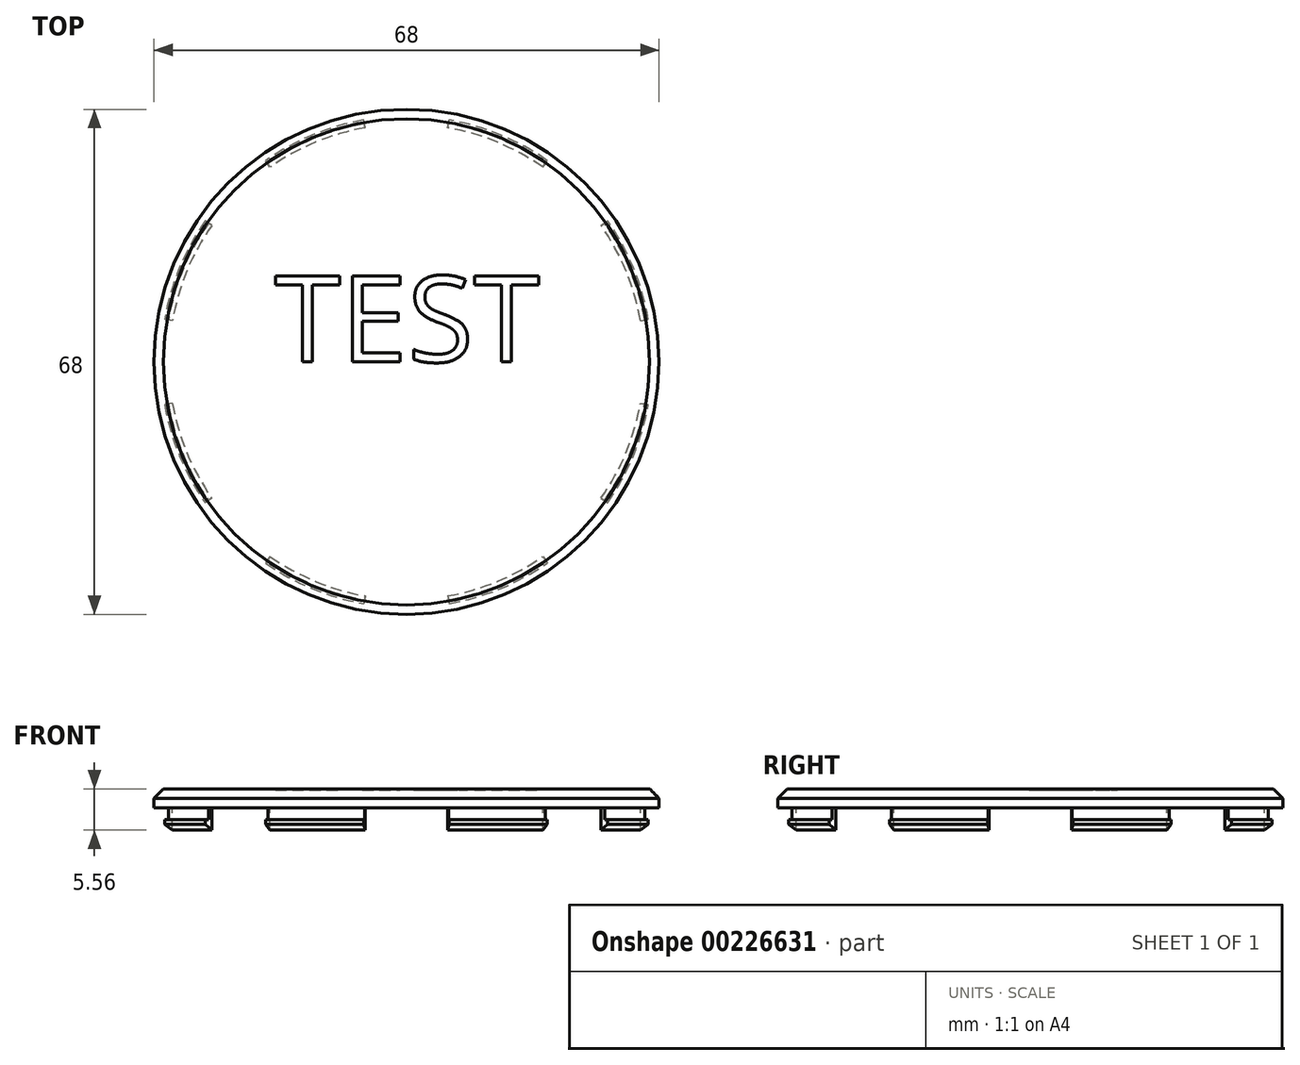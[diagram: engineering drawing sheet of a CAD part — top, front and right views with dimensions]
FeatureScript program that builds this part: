
annotation { "Feature Type Name" : "Feature", "Feature Type Description" : "" }
export const myFeature = defineFeature(function(context is Context, id is Id, definition is map)
    precondition{}
    {
        {
            var Q0;
            Q0=qCreatedBy(makeId("Top.planeOp"),FACE);
            var sketch = newSketch(context, id + "F0", { "sketchPlane" : qUnion([Q0])});
            skCircle(sketch, "E0", {"center": v(0, 0) * mm, "radius": 34 * mm});
            skSolve(sketch);
        }
        {
            var Q0;
            Q0=makeQuery(id+"F0.imprint","IMPRINT",FACE,{"disambiguationData":[TD([[makeQuery(id+"F0.imprint","IMPRINT",EDGE,{"derivedFrom":sQuery(id+"F0.wireOp",EDGE,"E0")}),1.0]])]});
            extrude(context, id + "F1", {"entities" : qUnion([Q0]), "depth" : 2.54 * mm});
        }
        {
            var Q0;
            Q0=makeQuery(id+"F1.opExtrude","CAP_EDGE",EDGE,{"disambiguationData":[OSD([sQuery(id+"F0.wireOp",EDGE,"E0")])],"isStart":false});
            chamfer(context, id + "F2", {"entities" : qUnion([Q0]), "width" : 1.27 * mm, "tangentPropagation" : true});
        }
        {
            var Q0;
            Q0=qCreatedBy(makeId("Front.planeOp"),FACE);
            var sketch = newSketch(context, id + "F3", { "sketchPlane" : qUnion([Q0])});
            skLineSegment(sketch, "E1", {"start": v(32.56, 0) * mm, "end": v(32.56, -1.61) * mm});
            skLineSegment(sketch, "E2", {"start": v(32.56, -1.61) * mm, "end": v(33.07, -1.61) * mm});
            skLineSegment(sketch, "E3", {"start": v(33.07, -1.61) * mm, "end": v(33.07, -2.24) * mm});
            skLineSegment(sketch, "E4", {"start": v(33.07, -2.24) * mm, "end": v(32, -3.02) * mm});
            skLineSegment(sketch, "E5", {"start": v(32, -3.02) * mm, "end": v(32, 0) * mm});
            skLineSegment(sketch, "E6", {"start": v(32, 0) * mm, "end": v(32.56, 0) * mm});
            skLineSegment(sketch, "E7", {"start": v(0, 0) * mm, "end": v(0, -19.48) * mm, "construction": true});
            skSolve(sketch);
        }
        {
            var Q0;
            Q0=qSketchRegion(id+"F3",true);
            var Q1;
            Q1=sQuery(id+"F3.wireOp",EDGE,"E7");
            revolve(context, id + "F4", {"operationType" : NewBodyOperationType.ADD, "entities" : qUnion([Q0]), "axis" : qUnion([Q1]), "revolveType" : RevolveType.FULL});
        }
        {
            var Q0;
            Q0=qCreatedBy(makeId("Top.planeOp"),FACE);
            var sketch = newSketch(context, id + "F5", { "sketchPlane" : qUnion([Q0])});
            skLineSegment(sketch, "E8", {"start": v(0, 0) * mm, "end": v(6.04, 34.27) * mm, "construction": true});
            skLineSegment(sketch, "E9", {"start": v(0, 0) * mm, "end": v(-6.04, 34.27) * mm, "construction": true});
            skLineSegment(sketch, "E10", {"start": v(0, 0) * mm, "end": v(-6.04, 34.27) * mm});
            skLineSegment(sketch, "E11", {"start": v(0, 0) * mm, "end": v(6.04, 34.27) * mm});
            skArc(sketch, "E12", {"start": v(6.04, 34.27) * mm, "mid": v(0, 34.8) * mm, "end": v(-6.04, 34.27) * mm});
            skArc(sketch, "E13.1.0", {"start": v(-19.96, 28.5) * mm, "mid": v(-24.6, 24.6) * mm, "end": v(-28.5, 19.96) * mm});
            skLineSegment(sketch, "E13.1.1", {"start": v(0, 0) * mm, "end": v(-19.96, 28.5) * mm});
            skLineSegment(sketch, "E13.1.2", {"start": v(0, 0) * mm, "end": v(-28.5, 19.96) * mm});
            skLineSegment(sketch, "E13.1.3", {"start": v(0, 0) * mm, "end": v(-28.5, 19.96) * mm, "construction": true});
            skLineSegment(sketch, "E13.1.4", {"start": v(0, 0) * mm, "end": v(-19.96, 28.5) * mm, "construction": true});
            skArc(sketch, "E13.2.0", {"start": v(-34.27, 6.04) * mm, "mid": v(-34.8, 0) * mm, "end": v(-34.27, -6.04) * mm});
            skLineSegment(sketch, "E13.2.1", {"start": v(0, 0) * mm, "end": v(-34.27, 6.04) * mm});
            skLineSegment(sketch, "E13.2.2", {"start": v(0, 0) * mm, "end": v(-34.27, -6.04) * mm});
            skLineSegment(sketch, "E13.2.3", {"start": v(0, 0) * mm, "end": v(-34.27, -6.04) * mm, "construction": true});
            skLineSegment(sketch, "E13.2.4", {"start": v(0, 0) * mm, "end": v(-34.27, 6.04) * mm, "construction": true});
            skArc(sketch, "E13.3.0", {"start": v(-28.5, -19.96) * mm, "mid": v(-24.6, -24.6) * mm, "end": v(-19.96, -28.5) * mm});
            skLineSegment(sketch, "E13.3.1", {"start": v(0, 0) * mm, "end": v(-28.5, -19.96) * mm});
            skLineSegment(sketch, "E13.3.2", {"start": v(0, 0) * mm, "end": v(-19.96, -28.5) * mm});
            skLineSegment(sketch, "E13.3.3", {"start": v(0, 0) * mm, "end": v(-19.96, -28.5) * mm, "construction": true});
            skLineSegment(sketch, "E13.3.4", {"start": v(0, 0) * mm, "end": v(-28.5, -19.96) * mm, "construction": true});
            skArc(sketch, "E13.4.0", {"start": v(-6.04, -34.27) * mm, "mid": v(0, -34.8) * mm, "end": v(6.04, -34.27) * mm});
            skLineSegment(sketch, "E13.4.1", {"start": v(0, 0) * mm, "end": v(-6.04, -34.27) * mm});
            skLineSegment(sketch, "E13.4.2", {"start": v(0, 0) * mm, "end": v(6.04, -34.27) * mm});
            skLineSegment(sketch, "E13.4.3", {"start": v(0, 0) * mm, "end": v(6.04, -34.27) * mm, "construction": true});
            skLineSegment(sketch, "E13.4.4", {"start": v(0, 0) * mm, "end": v(-6.04, -34.27) * mm, "construction": true});
            skArc(sketch, "E13.5.0", {"start": v(19.96, -28.5) * mm, "mid": v(24.6, -24.6) * mm, "end": v(28.5, -19.96) * mm});
            skLineSegment(sketch, "E13.5.1", {"start": v(0, 0) * mm, "end": v(19.96, -28.5) * mm});
            skLineSegment(sketch, "E13.5.2", {"start": v(0, 0) * mm, "end": v(28.5, -19.96) * mm});
            skLineSegment(sketch, "E13.5.3", {"start": v(0, 0) * mm, "end": v(28.5, -19.96) * mm, "construction": true});
            skLineSegment(sketch, "E13.5.4", {"start": v(0, 0) * mm, "end": v(19.96, -28.5) * mm, "construction": true});
            skArc(sketch, "E13.6.0", {"start": v(34.27, -6.04) * mm, "mid": v(34.8, 0) * mm, "end": v(34.27, 6.04) * mm});
            skLineSegment(sketch, "E13.6.1", {"start": v(0, 0) * mm, "end": v(34.27, -6.04) * mm});
            skLineSegment(sketch, "E13.6.2", {"start": v(0, 0) * mm, "end": v(34.27, 6.04) * mm});
            skLineSegment(sketch, "E13.6.3", {"start": v(0, 0) * mm, "end": v(34.27, 6.04) * mm, "construction": true});
            skLineSegment(sketch, "E13.6.4", {"start": v(0, 0) * mm, "end": v(34.27, -6.04) * mm, "construction": true});
            skArc(sketch, "E13.7.0", {"start": v(28.5, 19.96) * mm, "mid": v(24.6, 24.6) * mm, "end": v(19.96, 28.5) * mm});
            skLineSegment(sketch, "E13.7.1", {"start": v(0, 0) * mm, "end": v(28.5, 19.96) * mm});
            skLineSegment(sketch, "E13.7.2", {"start": v(0, 0) * mm, "end": v(19.96, 28.5) * mm});
            skLineSegment(sketch, "E13.7.3", {"start": v(0, 0) * mm, "end": v(19.96, 28.5) * mm, "construction": true});
            skLineSegment(sketch, "E13.7.4", {"start": v(0, 0) * mm, "end": v(28.5, 19.96) * mm, "construction": true});
            skSolve(sketch);
        }
        {
            var Q0;
            Q0=makeQuery(id+"F5.imprint","IMPRINT",FACE,{"disambiguationData":[TD([[makeQuery(id+"F5.imprint","IMPRINT",EDGE,{"derivedFrom":sQuery(id+"F5.wireOp",EDGE,"E10")}),-1.0]])]});
            var Q1;
            Q1=makeQuery(id+"F5.imprint","IMPRINT",FACE,{"disambiguationData":[TD([[makeQuery(id+"F5.imprint","IMPRINT",EDGE,{"derivedFrom":sQuery(id+"F5.wireOp",EDGE,"E13.1.0")}),1.0]])]});
            var Q2;
            Q2=makeQuery(id+"F5.imprint","IMPRINT",FACE,{"disambiguationData":[TD([[makeQuery(id+"F5.imprint","IMPRINT",EDGE,{"derivedFrom":sQuery(id+"F5.wireOp",EDGE,"E13.2.0")}),1.0]])]});
            var Q3;
            Q3=makeQuery(id+"F5.imprint","IMPRINT",FACE,{"disambiguationData":[TD([[makeQuery(id+"F5.imprint","IMPRINT",EDGE,{"derivedFrom":sQuery(id+"F5.wireOp",EDGE,"E13.3.0")}),1.0]])]});
            var Q4;
            Q4=makeQuery(id+"F5.imprint","IMPRINT",FACE,{"disambiguationData":[TD([[makeQuery(id+"F5.imprint","IMPRINT",EDGE,{"derivedFrom":sQuery(id+"F5.wireOp",EDGE,"E13.4.0")}),1.0]])]});
            var Q5;
            Q5=makeQuery(id+"F5.imprint","IMPRINT",FACE,{"disambiguationData":[TD([[makeQuery(id+"F5.imprint","IMPRINT",EDGE,{"derivedFrom":sQuery(id+"F5.wireOp",EDGE,"E13.5.0")}),1.0]])]});
            var Q6;
            Q6=makeQuery(id+"F5.imprint","IMPRINT",FACE,{"disambiguationData":[TD([[makeQuery(id+"F5.imprint","IMPRINT",EDGE,{"derivedFrom":sQuery(id+"F5.wireOp",EDGE,"E13.6.0")}),1.0]])]});
            var Q7;
            Q7=makeQuery(id+"F5.imprint","IMPRINT",FACE,{"disambiguationData":[TD([[makeQuery(id+"F5.imprint","IMPRINT",EDGE,{"derivedFrom":sQuery(id+"F5.wireOp",EDGE,"E13.7.0")}),1.0]])]});
            extrude(context, id + "F6", {"entities" : qUnion([Q0, Q1, Q2, Q3, Q4, Q5, Q6, Q7]), "operationType" : NewBodyOperationType.REMOVE, "oppositeDirection" : true, "depth" : 25.4 * mm});
        }
        {
            var Q0;
            Q0=makeQuery(id+"F1.opExtrude","CAP_FACE",FACE,{"disambiguationData":[OSD([sQuery(id+"F0.wireOp",EDGE,"E0")])],"isStart":false});
            var sketch = newSketch(context, id + "F7", { "sketchPlane" : qUnion([Q0])});
            skText(sketch, "E14", { "text": "TEST", "fontName": "OpenSans-Regular.ttf"});
            const initialGuessF7  = {"E14": [-0.0178, 0, 1, 0, 0.01164]};
            skSetInitialGuess(sketch, initialGuessF7);
            skSolve(sketch);
        }
        {
            var Q0;
            Q0=qSketchRegion(id+"F7",true);
            extrude(context, id + "F8", {"entities" : qUnion([Q0]), "operationType" : NewBodyOperationType.REMOVE, "oppositeDirection" : true, "depth" : 0.13 * mm});
        }
    });
